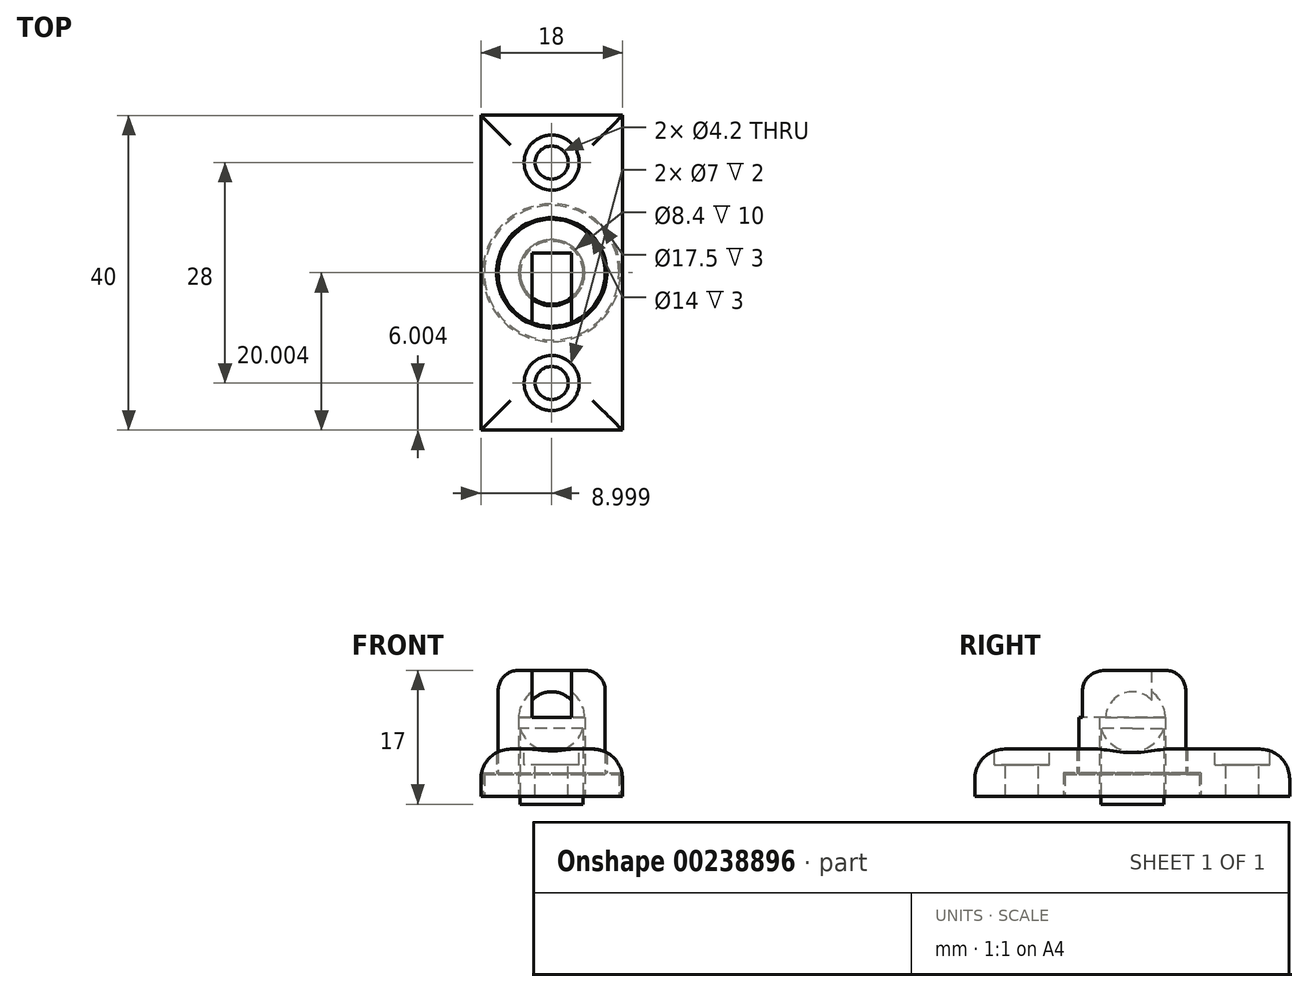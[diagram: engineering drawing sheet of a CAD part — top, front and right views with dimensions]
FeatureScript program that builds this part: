
annotation { "Feature Type Name" : "Feature", "Feature Type Description" : "" }
export const myFeature = defineFeature(function(context is Context, id is Id, definition is map)
    precondition{}
    {
        {
            var Q0;
            Q0=qCreatedBy(makeId("Top.planeOp"),FACE);
            var sketch = newSketch(context, id + "F0", { "sketchPlane" : qUnion([Q0])});
            skLineSegment(sketch, "E0.bottom", {"start": v(-6.67, 23.32) * mm, "end": v(11.33, 23.32) * mm});
            skLineSegment(sketch, "E0.top", {"start": v(-6.67, -16.68) * mm, "end": v(11.33, -16.68) * mm});
            skLineSegment(sketch, "E0.left", {"start": v(-6.67, 23.32) * mm, "end": v(-6.67, -16.68) * mm});
            skLineSegment(sketch, "E0.right", {"start": v(11.33, 23.32) * mm, "end": v(11.33, -16.68) * mm});
            skSolve(sketch);
        }
        {
            var Q0;
            Q0=makeQuery(id+"F0.imprint","IMPRINT",FACE,{"disambiguationData":[TD([[makeQuery(id+"F0.imprint","IMPRINT",EDGE,{"derivedFrom":sQuery(id+"F0.wireOp",EDGE,"E0.bottom")}),-1.0]])]});
            extrude(context, id + "F1", {"entities" : qUnion([Q0]), "depth" : 6 * mm});
        }
        {
            var Q0;
            Q0=makeQuery(id+"F1.opExtrude","CAP_FACE",FACE,{"disambiguationData":[OSD([sQuery(id+"F0.wireOp",EDGE,"E0.bottom"),sQuery(id+"F0.wireOp",EDGE,"E0.top"),sQuery(id+"F0.wireOp",EDGE,"E0.left"),sQuery(id+"F0.wireOp",EDGE,"E0.right")])],"isStart":true});
            var sketch = newSketch(context, id + "F2", { "sketchPlane" : qUnion([Q0])});
            skLineSegment(sketch, "E1", {"start": v(11.33, -3.32) * mm, "end": v(-6.67, -3.32) * mm, "construction": true});
            skLineSegment(sketch, "E2", {"start": v(2.33, -23.32) * mm, "end": v(2.33, 16.68) * mm, "construction": true});
            skPoint(sketch, "E3", {"position": v(2.33, -3.32) * mm});
            skCircle(sketch, "E4", {"center": v(2.33, -3.32) * mm, "radius": 8.75 * mm});
            skSolve(sketch);
        }
        {
            var Q0;
            Q0=makeQuery(id+"F2.imprint","IMPRINT",FACE,{"disambiguationData":[TD([[makeQuery(id+"F2.imprint","IMPRINT",EDGE,{"derivedFrom":sQuery(id+"F2.wireOp",EDGE,"E4")}),1.0]])]});
            extrude(context, id + "F3", {"entities" : qUnion([Q0]), "operationType" : NewBodyOperationType.REMOVE, "oppositeDirection" : true, "depth" : 3 * mm});
        }
        {
            var Q0;
            Q0=makeQuery(id+"F1.opExtrude","CAP_FACE",FACE,{"disambiguationData":[OSD([sQuery(id+"F0.wireOp",EDGE,"E0.bottom"),sQuery(id+"F0.wireOp",EDGE,"E0.top"),sQuery(id+"F0.wireOp",EDGE,"E0.left"),sQuery(id+"F0.wireOp",EDGE,"E0.right")])],"isStart":true});
            var sketch = newSketch(context, id + "F4", { "sketchPlane" : qUnion([Q0])});
            skCircle(sketch, "E5", {"center": v(2.33, -3.32) * mm, "radius": 7 * mm});
            skSolve(sketch);
        }
        {
            var Q0;
            Q0=makeQuery(id+"F4.imprint","IMPRINT",FACE,{"disambiguationData":[TD([[makeQuery(id+"F4.imprint","IMPRINT",EDGE,{"derivedFrom":sQuery(id+"F4.wireOp",EDGE,"E5")}),1.0]])]});
            extrude(context, id + "F5", {"entities" : qUnion([Q0]), "operationType" : NewBodyOperationType.REMOVE, "endBound" : BoundingType.THROUGH_ALL, "oppositeDirection" : true, "depth" : 25 * mm});
        }
        {
            var Q0;
            Q0=makeQuery(id+"F1.opExtrude","CAP_FACE",FACE,{"disambiguationData":[OSD([sQuery(id+"F0.wireOp",EDGE,"E0.bottom"),sQuery(id+"F0.wireOp",EDGE,"E0.top"),sQuery(id+"F0.wireOp",EDGE,"E0.left"),sQuery(id+"F0.wireOp",EDGE,"E0.right")])],"isStart":true});
            var sketch = newSketch(context, id + "F6", { "sketchPlane" : qUnion([Q0])});
            skCircle(sketch, "E6.0", {"center": v(2.33, -3.32) * mm, "radius": 8.55 * mm});
            skSolve(sketch);
        }
        {
            var Q0;
            Q0=makeQuery(id+"F6.imprint","IMPRINT",FACE,{"disambiguationData":[TD([[makeQuery(id+"F6.imprint","IMPRINT",EDGE,{"derivedFrom":sQuery(id+"F6.wireOp",EDGE,"E6.0")}),1.0]])]});
            extrude(context, id + "F7", {"entities" : qUnion([Q0]), "oppositeDirection" : true, "depth" : 2.8 * mm});
        }
        {
            var Q0;
            Q0=makeQuery(id+"F1.opExtrude","CAP_FACE",FACE,{"disambiguationData":[OSD([sQuery(id+"F0.wireOp",EDGE,"E0.bottom"),sQuery(id+"F0.wireOp",EDGE,"E0.top"),sQuery(id+"F0.wireOp",EDGE,"E0.left"),sQuery(id+"F0.wireOp",EDGE,"E0.right")])],"isStart":true});
            var sketch = newSketch(context, id + "F8", { "sketchPlane" : qUnion([Q0])});
            skCircle(sketch, "E7", {"center": v(2.33, -3.32) * mm, "radius": 6.8 * mm});
            skSolve(sketch);
        }
        {
            var Q0;
            Q0=makeQuery(id+"F8.imprint","IMPRINT",FACE,{"disambiguationData":[TD([[makeQuery(id+"F8.imprint","IMPRINT",EDGE,{"derivedFrom":sQuery(id+"F8.wireOp",EDGE,"E7")}),1.0]])]});
            extrude(context, id + "F9", {"entities" : qUnion([Q0]), "operationType" : NewBodyOperationType.ADD, "oppositeDirection" : true, "depth" : 16 * mm});
        }
        {
            var Q0;
            Q0=makeQuery(id+"F1.opExtrude","CAP_FACE",FACE,{"disambiguationData":[OSD([sQuery(id+"F0.wireOp",EDGE,"E0.bottom"),sQuery(id+"F0.wireOp",EDGE,"E0.top"),sQuery(id+"F0.wireOp",EDGE,"E0.left"),sQuery(id+"F0.wireOp",EDGE,"E0.right")])],"isStart":true});
            var sketch = newSketch(context, id + "F10", { "sketchPlane" : qUnion([Q0])});
            skCircle(sketch, "E8", {"center": v(2.33, -3.32) * mm, "radius": 4.2 * mm});
            skSolve(sketch);
        }
        {
            var Q0;
            Q0 = qSketchRegion(id + "F10", true);
            extrude(context, id + "F11", {"entities" : qUnion([Q0]), "operationType" : NewBodyOperationType.REMOVE, "oppositeDirection" : true, "depth" : 10 * mm});
        }
        {
            var Q0;
            Q0=makeQuery(id+"F1.opExtrude","CAP_FACE",FACE,{"disambiguationData":[OSD([sQuery(id+"F0.wireOp",EDGE,"E0.bottom"),sQuery(id+"F0.wireOp",EDGE,"E0.top"),sQuery(id+"F0.wireOp",EDGE,"E0.left"),sQuery(id+"F0.wireOp",EDGE,"E0.right")])],"isStart":true});
            var sketch = newSketch(context, id + "F12", { "sketchPlane" : qUnion([Q0])});
            skCircle(sketch, "E9", {"center": v(2.33, -3.32) * mm, "radius": 4 * mm});
            skSolve(sketch);
        }
        {
            var Q0;
            Q0=makeQuery(id+"F12.imprint","IMPRINT",FACE,{"disambiguationData":[TD([[makeQuery(id+"F12.imprint","IMPRINT",EDGE,{"derivedFrom":sQuery(id+"F12.wireOp",EDGE,"E9")}),1.0]])]});
            extrude(context, id + "F13", {"entities" : qUnion([Q0]), "oppositeDirection" : true, "depth" : 9.9 * mm, "hasSecondDirection" : true, "secondDirectionOppositeDirection" : false, "secondDirectionDepth" : 1 * mm});
        }
        {
            var Q0;
            Q0=makeQuery(id+"F13.opExtrude","CAP_FACE",FACE,{"disambiguationData":[OSD([sQuery(id+"F12.wireOp",EDGE,"E9")])],"isStart":false});
            var sketch = newSketch(context, id + "F14", { "sketchPlane" : qUnion([Q0])});
            skArc(sketch, "E10.0", {"start": v(-1.6, 1.85) * mm, "mid": v(3.8, -0.6) * mm, "end": v(6.26, 4.8) * mm});
            skLineSegment(sketch, "E11", {"start": v(2.33, 3.32) * mm, "end": v(6.26, 4.8) * mm});
            skLineSegment(sketch, "E12", {"start": v(2.33, 3.32) * mm, "end": v(-1.6, 1.85) * mm});
            skSolve(sketch);
        }
        {
            var Q0;
            Q0 = qSketchRegion(id + "F14", true);
            var Q1;
            Q1=sQuery(id+"F14.wireOp",EDGE,"E12");
            revolve(context, id + "F15", {"operationType" : NewBodyOperationType.REMOVE, "entities" : qUnion([Q0]), "axis" : qUnion([Q1]), "revolveType" : RevolveType.FULL});
        }
        {
            var Q0;
            Q0=makeQuery(id+"F9.opExtrude","CAP_FACE",FACE,{"disambiguationData":[OSD([sQuery(id+"F8.wireOp",EDGE,"E7")])],"isStart":false});
            var sketch = newSketch(context, id + "F16", { "sketchPlane" : qUnion([Q0])});
            skLineSegment(sketch, "E13.bottom", {"start": v(4.83, 5.82) * mm, "end": v(-0.17, 5.82) * mm});
            skLineSegment(sketch, "E13.top", {"start": v(4.83, -17.38) * mm, "end": v(-0.17, -17.38) * mm});
            skLineSegment(sketch, "E13.left", {"start": v(4.83, 5.82) * mm, "end": v(4.83, -17.38) * mm});
            skLineSegment(sketch, "E13.right", {"start": v(-0.17, 5.82) * mm, "end": v(-0.17, -17.38) * mm});
            skSolve(sketch);
        }
        {
            var Q0;
            Q0 = qSketchRegion(id + "F16", true);
            extrude(context, id + "F17", {"entities" : qUnion([Q0]), "operationType" : NewBodyOperationType.REMOVE, "oppositeDirection" : true, "depth" : 6 * mm});
        }
        {
            var Q0;
            Q0=makeQuery(id+"F1.opExtrude","CAP_FACE",FACE,{"disambiguationData":[OSD([sQuery(id+"F0.wireOp",EDGE,"E0.bottom"),sQuery(id+"F0.wireOp",EDGE,"E0.top"),sQuery(id+"F0.wireOp",EDGE,"E0.left"),sQuery(id+"F0.wireOp",EDGE,"E0.right")])],"isStart":false});
            var sketch = newSketch(context, id + "F18", { "sketchPlane" : qUnion([Q0])});
            skLineSegment(sketch, "E14", {"start": v(-6.67, 17.32) * mm, "end": v(11.33, 17.32) * mm, "construction": true});
            skPoint(sketch, "E15", {"position": v(2.33, 17.32) * mm});
            skLineSegment(sketch, "E16", {"start": v(11.33, 3.32) * mm, "end": v(-6.67, 3.32) * mm, "construction": true});
            skPoint(sketch, "E17.MirrorP", {"position": v(2.33, -10.68) * mm});
            skSolve(sketch);
        }
        {
            var Q0;
            Q0=sQuery(id+"F18.wireOp",VERTEX,"E15");
            var Q1;
            Q1=makeQuery(id+"F1.opExtrude","SWEPT_BODY",BODY,{"disambiguationData":[OSD([sQuery(id+"F0.wireOp",EDGE,"E0.bottom"),sQuery(id+"F0.wireOp",EDGE,"E0.top"),sQuery(id+"F0.wireOp",EDGE,"E0.left"),sQuery(id+"F0.wireOp",EDGE,"E0.right")])]});
            hole(context, id + "F19", {"style" : HoleStyle.C_BORE, "endStyle" : HoleEndStyle.THROUGH, "holeDiameter" : 4.2 * mm, "cBoreDiameter" : 7 * mm, "cBoreDepth" : 2 * mm, "locations" : qUnion([Q0]), "scope" : qUnion([Q1]), "isTappedThrough" : true});
        }
        {
            var Q0;
            Q0=sQuery(id+"F18.wireOp",VERTEX,"E17.MirrorP");
            var Q1;
            Q1=makeQuery(id+"F1.opExtrude","SWEPT_BODY",BODY,{"disambiguationData":[OSD([sQuery(id+"F0.wireOp",EDGE,"E0.bottom"),sQuery(id+"F0.wireOp",EDGE,"E0.top"),sQuery(id+"F0.wireOp",EDGE,"E0.left"),sQuery(id+"F0.wireOp",EDGE,"E0.right")])]});
            hole(context, id + "F20", {"style" : HoleStyle.C_BORE, "endStyle" : HoleEndStyle.THROUGH, "holeDiameter" : 4.2 * mm, "cBoreDiameter" : 7 * mm, "cBoreDepth" : 2 * mm, "locations" : qUnion([Q0]), "scope" : qUnion([Q1]), "isTappedThrough" : true});
        }
        {
            var Q0;
            Q0=makeQuery(id+"F1.opExtrude","CAP_EDGE",EDGE,{"disambiguationData":[OSD([sQuery(id+"F0.wireOp",EDGE,"E0.right")])],"isStart":false});
            var Q1;
            Q1=makeQuery(id+"F1.opExtrude","CAP_EDGE",EDGE,{"disambiguationData":[OSD([sQuery(id+"F0.wireOp",EDGE,"E0.top")])],"isStart":false});
            var Q2;
            Q2=makeQuery(id+"F1.opExtrude","CAP_EDGE",EDGE,{"disambiguationData":[OSD([sQuery(id+"F0.wireOp",EDGE,"E0.left")])],"isStart":false});
            var Q3;
            Q3=makeQuery(id+"F1.opExtrude","CAP_EDGE",EDGE,{"disambiguationData":[OSD([sQuery(id+"F0.wireOp",EDGE,"E0.bottom")])],"isStart":false});
            fillet(context, id + "F21", {"entities" : qUnion([Q0, Q1, Q2, Q3]), "radius" : 3.8 * mm, "tangentPropagation" : true, "allowEdgeOverflow" : false});
        }
        {
            var Q0;
            Q0=makeQuery(id+"F9.opExtrude","CAP_EDGE",EDGE,{"disambiguationData":[OSD([sQuery(id+"F8.wireOp",EDGE,"E7")])],"isStart":false});
            fillet(context, id + "F22", {"entities" : qUnion([Q0]), "radius" : 2.6 * mm, "tangentPropagation" : true, "allowEdgeOverflow" : false});
        }
    });
